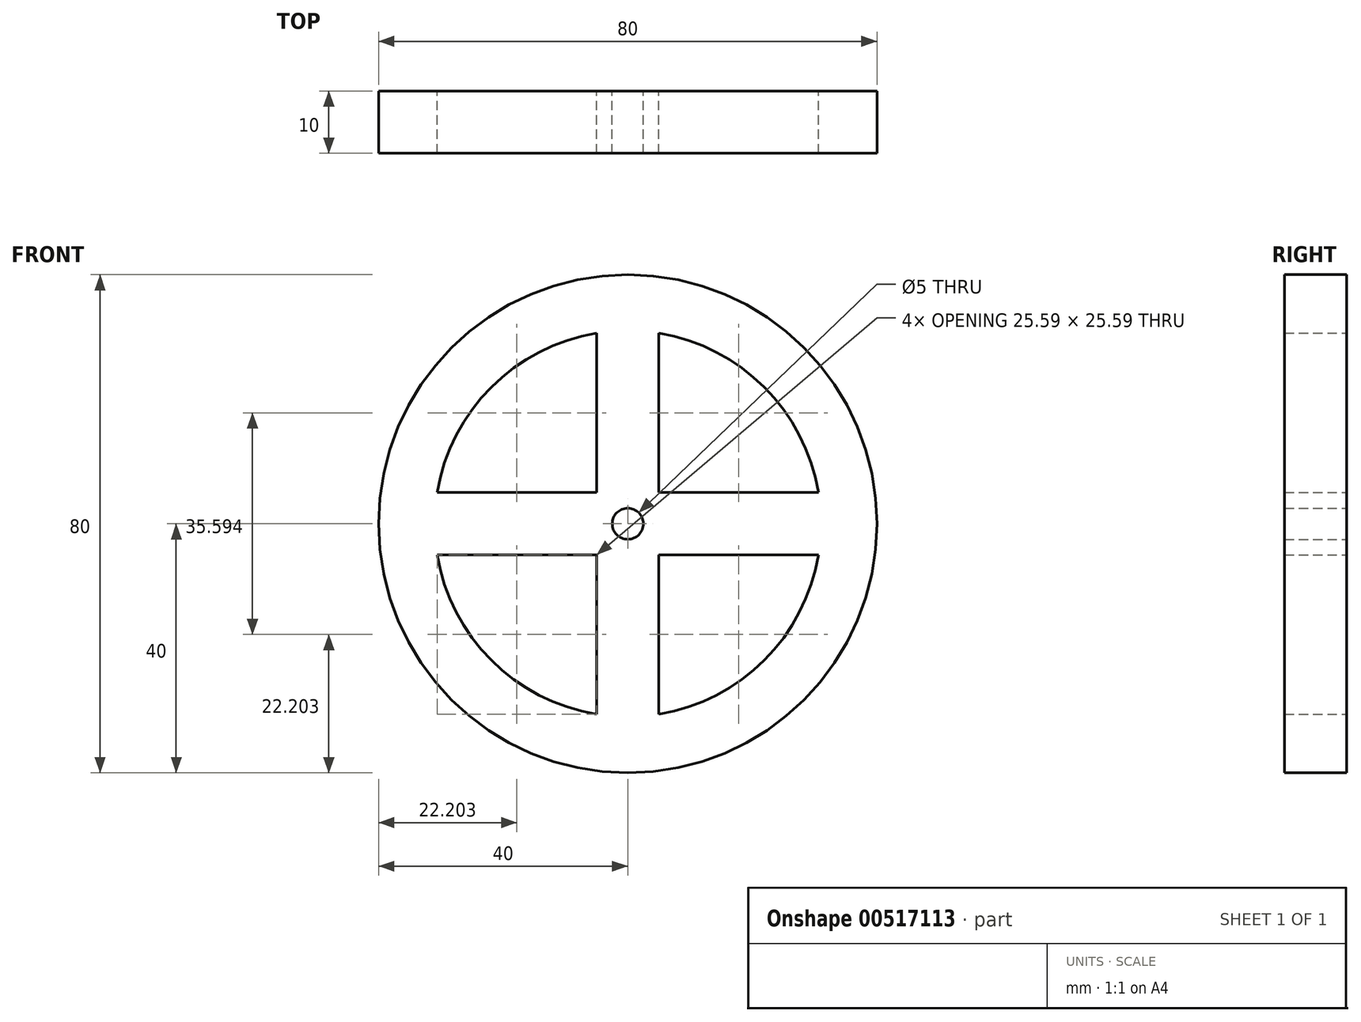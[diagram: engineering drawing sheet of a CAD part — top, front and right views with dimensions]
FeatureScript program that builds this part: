
annotation { "Feature Type Name" : "Feature", "Feature Type Description" : "" }
export const myFeature = defineFeature(function(context is Context, id is Id, definition is map)
    precondition{}
    {
        {
            var Q0;
            Q0=qCreatedBy(makeId("Front.planeOp"),FACE);
            var sketch = newSketch(context, id + "F0", { "sketchPlane" : qUnion([Q0])});
            skArc(sketch, "E0", {"start": v(5.6, 5) * mm, "mid": v(5.3, 5.3) * mm, "end": v(5, 5.6) * mm});
            skArc(sketch, "E1", {"start": v(-5, 30.6) * mm, "mid": v(-21.92, 21.92) * mm, "end": v(-30.6, 5) * mm});
            skCircle(sketch, "E2", {"center": v(0, 0) * mm, "radius": 40 * mm});
            skCircle(sketch, "E3", {"center": v(0, 0) * mm, "radius": 2.5 * mm});
            skLineSegment(sketch, "E4.0", {"start": v(5, 5) * mm, "end": v(5, 30.6) * mm});
            skLineSegment(sketch, "E5.0", {"start": v(-5, 5) * mm, "end": v(-5, 30.6) * mm});
            skLineSegment(sketch, "E6.0", {"start": v(5, 5) * mm, "end": v(30.6, 5) * mm});
            skLineSegment(sketch, "E7.0", {"start": v(5, -5) * mm, "end": v(30.6, -5) * mm});
            skLineSegment(sketch, "E8.0", {"start": v(-5, 5) * mm, "end": v(-30.6, 5) * mm});
            skLineSegment(sketch, "E9.0", {"start": v(-5, 5) * mm, "end": v(-5.6, 5) * mm});
            skLineSegment(sketch, "E10.0", {"start": v(-5, -5) * mm, "end": v(-30.6, -5) * mm});
            skLineSegment(sketch, "E11.0", {"start": v(5, -5) * mm, "end": v(5, -30.6) * mm});
            skLineSegment(sketch, "E12.0", {"start": v(-5, -5) * mm, "end": v(-5, -30.6) * mm});
            skArc(sketch, "E13.trimOffspring", {"start": v(5, -30.6) * mm, "mid": v(21.92, -21.92) * mm, "end": v(30.6, -5) * mm});
            skArc(sketch, "E14.trimOffspring", {"start": v(-5, 5.6) * mm, "mid": v(-5.3, 5.3) * mm, "end": v(-5.6, 5) * mm});
            skArc(sketch, "E15.trimOffspring", {"start": v(-5.6, -5) * mm, "mid": v(-5.3, -5.3) * mm, "end": v(-5, -5.6) * mm});
            skArc(sketch, "E16.trimOffspring", {"start": v(5, -5.6) * mm, "mid": v(5.3, -5.3) * mm, "end": v(5.6, -5) * mm});
            skArc(sketch, "E17.trimOffspring", {"start": v(-30.6, -5) * mm, "mid": v(-21.92, -21.92) * mm, "end": v(-5, -30.6) * mm});
            skArc(sketch, "E18.trimOffspring", {"start": v(30.6, 5) * mm, "mid": v(21.92, 21.92) * mm, "end": v(5, 30.6) * mm});
            skSolve(sketch);
        }
        {
            var Q0;
            {var subQ12=sQuery(id+"F0.wireOp",EDGE,"E1");Q0=makeQuery(id+"F0.imprint","IMPRINT",FACE,{"disambiguationData":[TD([[makeQuery(id+"F0.imprint","IMPRINT",EDGE,{"derivedFrom":subQ12}),-1.0]])]});}
            extrude(context, id + "F1", {"entities" : qUnion([Q0]), "depth" : 10 * mm, "offsetDistance" : 25 * mm});
        }
    });
